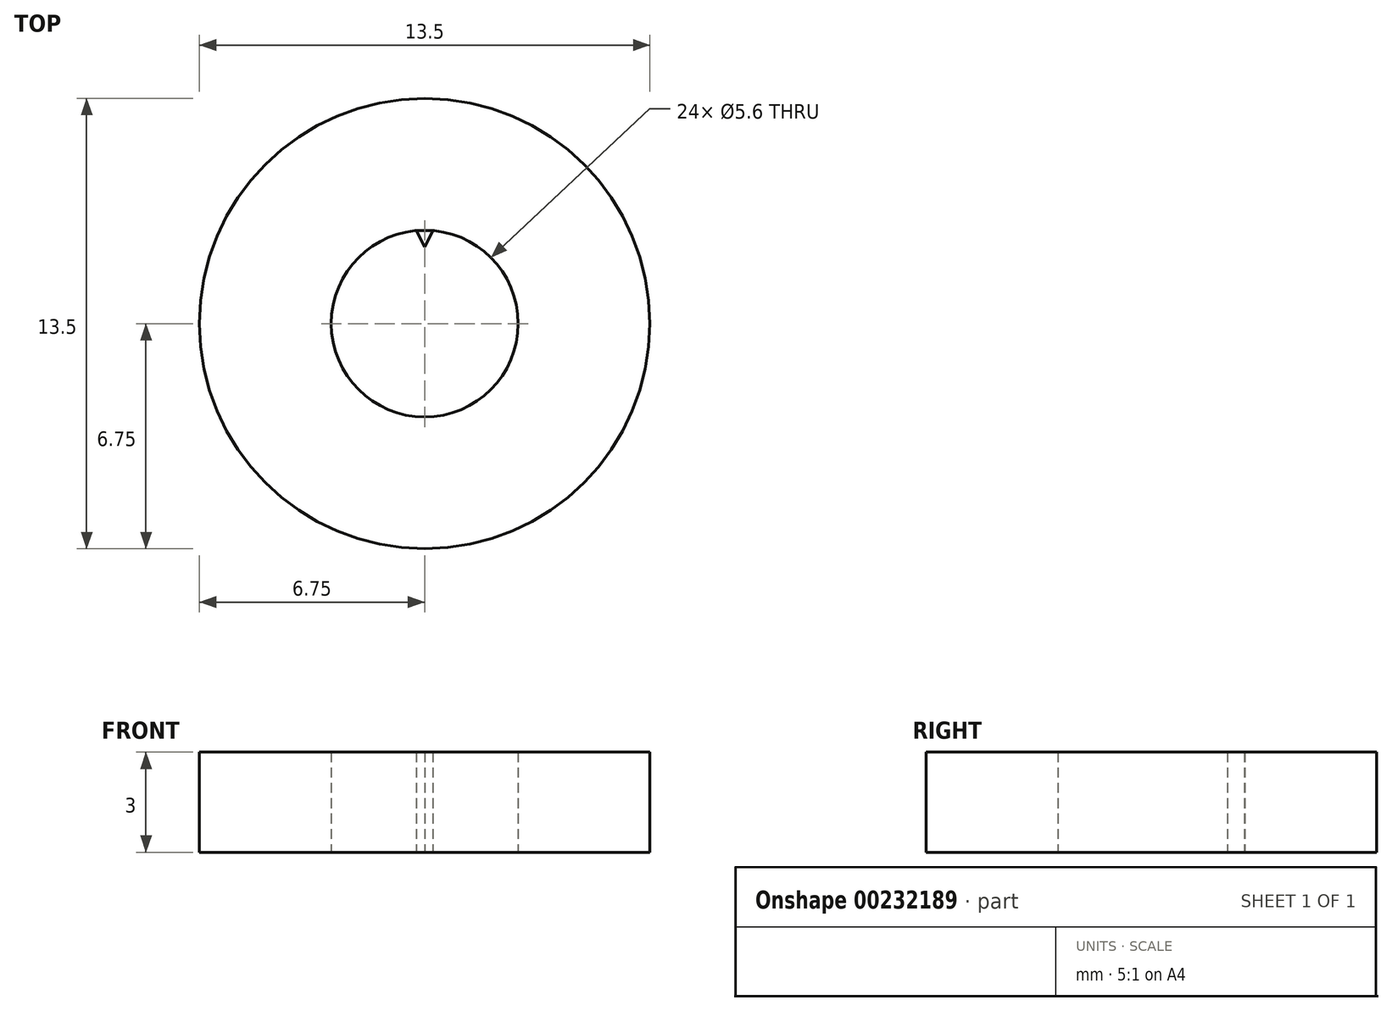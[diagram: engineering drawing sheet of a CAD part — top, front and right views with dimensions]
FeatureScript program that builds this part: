
annotation { "Feature Type Name" : "Feature", "Feature Type Description" : "" }
export const myFeature = defineFeature(function(context is Context, id is Id, definition is map)
    precondition{}
    {
        {
            var Q0;
            Q0=qCreatedBy(makeId("Top.planeOp"),FACE);
            var sketch = newSketch(context, id + "F0", { "sketchPlane" : qUnion([Q0])});
            skCircle(sketch, "E0", {"center": v(0, 0) * mm, "radius": 6.75 * mm});
            skCircle(sketch, "E1", {"center": v(0, 0) * mm, "radius": 2.8 * mm});
            skLineSegment(sketch, "E2", {"start": v(-0.25, 2.79) * mm, "end": v(0, 2.29) * mm});
            skLineSegment(sketch, "E3", {"start": v(0, 2.29) * mm, "end": v(0.25, 2.79) * mm});
            skLineSegment(sketch, "E4", {"start": v(0.25, 2.79) * mm, "end": v(-0.25, 2.79) * mm});
            skLineSegment(sketch, "E5", {"start": v(0, 2.29) * mm, "end": v(0, 2.79) * mm, "construction": true});
            skLineSegment(sketch, "E6.bottom", {"start": v(-0.25, 2.79) * mm, "end": v(0.25, 2.79) * mm});
            skLineSegment(sketch, "E6.top", {"start": v(-0.25, 3.29) * mm, "end": v(0.25, 3.29) * mm});
            skLineSegment(sketch, "E6.left", {"start": v(-0.25, 2.79) * mm, "end": v(-0.25, 3.29) * mm});
            skLineSegment(sketch, "E6.right", {"start": v(0.25, 2.79) * mm, "end": v(0.25, 3.29) * mm});
            skSolve(sketch);
        }
        {
            var Q0;
            Q0=qSketchRegion(id+"F0",true);
            var Q1;
            Q1=makeQuery(id+"F0.imprint","IMPRINT",FACE,{"disambiguationData":[TD([[makeQuery(id+"F0.imprint","IMPRINT",EDGE,{"derivedFrom":sQuery(id+"F0.wireOp",EDGE,"E6.top")}),-1.0]])]});
            var Q2;
            Q2=makeQuery(id+"F0.imprint","IMPRINT",FACE,{"disambiguationData":[TD([[makeQuery(id+"F0.imprint","IMPRINT",EDGE,{"derivedFrom":sQuery(id+"F0.wireOp",EDGE,"E2")}),1.0]])]});
            var Q3;
            {var subQ0=sQuery(id+"F0.wireOp",EDGE,"E6.bottom");Q3=makeQuery(id+"F0.imprint","IMPRINT",FACE,{"disambiguationData":[TD([[makeQuery(id+"F0.imprint","IMPRINT",EDGE,{"derivedFrom":subQ0}),1.0]])]});}
            extrude(context, id + "F1", {"entities" : qUnion([Q0, Q1, Q2, Q3]), "depth" : 3 * mm});
        }
        {
            var Q0;
            Q0=makeQuery(id+"F1.opExtrude","SWEPT_BODY",BODY,{"disambiguationData":[OSD([sQuery(id+"F0.wireOp",EDGE,"E0"),sQuery(id+"F0.wireOp",EDGE,"E1"),sQuery(id+"F0.wireOp",EDGE,"E2"),sQuery(id+"F0.wireOp",EDGE,"E3")])]});
            var Q1;
            Q1=makeQuery(id+"F1.opExtrude","SWEPT_FACE",FACE,{"disambiguationData":[OSD([sQuery(id+"F0.wireOp",EDGE,"E0")])]});
            circularPattern(context, id + "F2", {"operationType" : NewBodyOperationType.ADD, "entities" : qUnion([Q0]), "axis" : qUnion([Q1]), "angle" : 360 * degree, "instanceCount" : 24, "equalSpace" : true});
        }
    });
